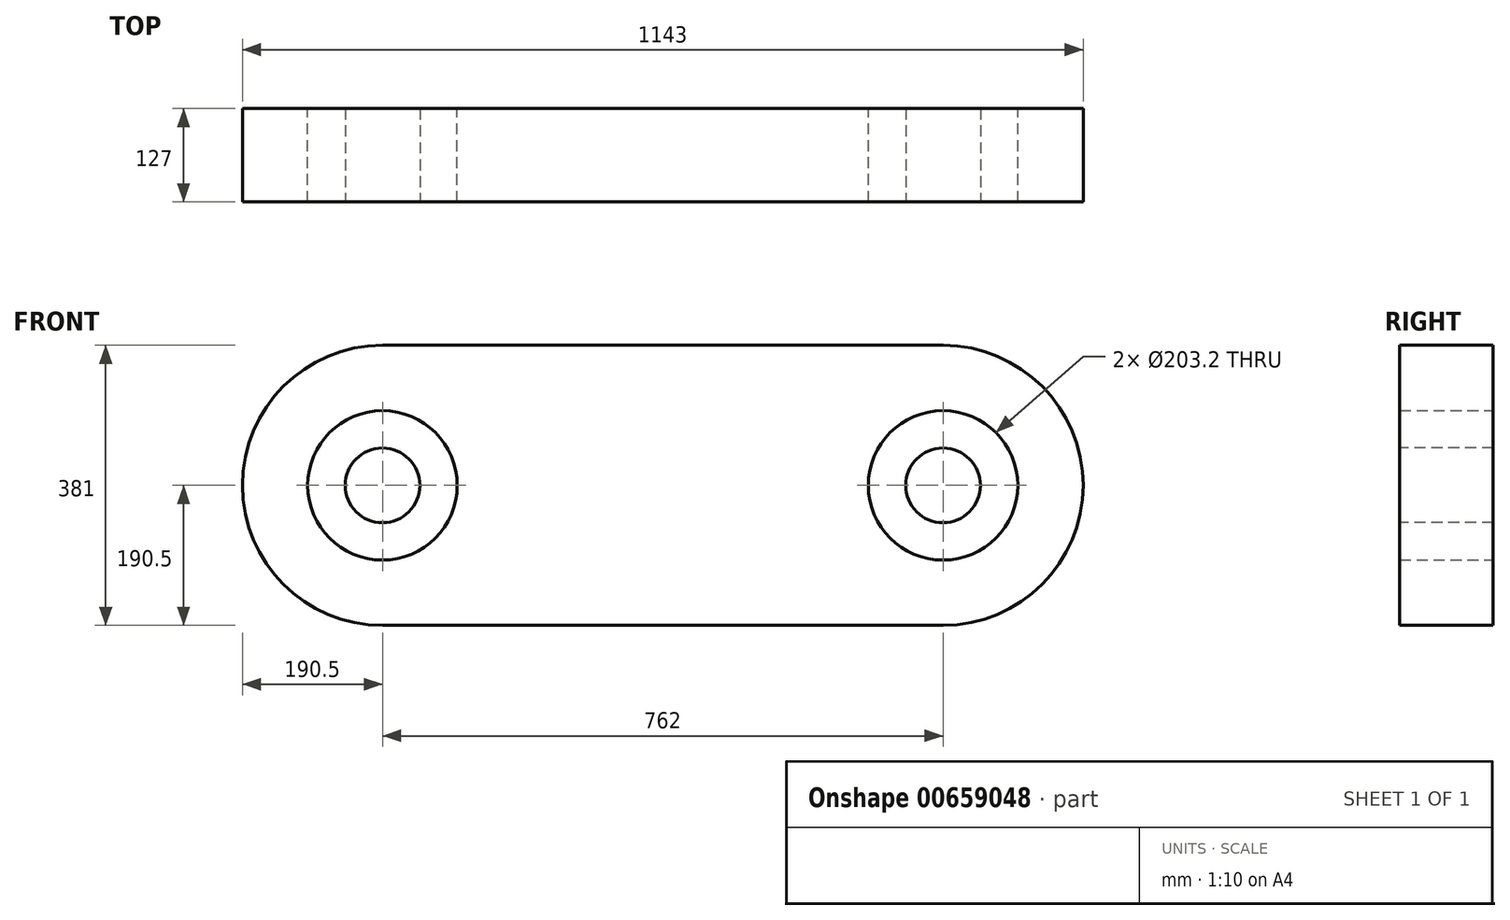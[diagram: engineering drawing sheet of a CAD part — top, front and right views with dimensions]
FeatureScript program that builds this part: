
annotation { "Feature Type Name" : "Feature", "Feature Type Description" : "" }
export const myFeature = defineFeature(function(context is Context, id is Id, definition is map)
    precondition{}
    {
        {
            var Q0;
            Q0=qCreatedBy(makeId("Front.planeOp"),FACE);
            var sketch = newSketch(context, id + "F0", { "sketchPlane" : qUnion([Q0])});
            skArc(sketch, "E0", {"start": v(-381, 190.5) * mm, "mid": v(-571.5, 0) * mm, "end": v(-381, -190.5) * mm});
            skArc(sketch, "E1", {"start": v(381, -190.5) * mm, "mid": v(571.5, 0) * mm, "end": v(381, 190.5) * mm});
            skLineSegment(sketch, "E2", {"start": v(-381, 190.5) * mm, "end": v(381, 190.5) * mm});
            skLineSegment(sketch, "E3", {"start": v(-381, -190.5) * mm, "end": v(381, -190.5) * mm});
            skCircle(sketch, "E4", {"center": v(-381, 0) * mm, "radius": 50.8 * mm});
            skCircle(sketch, "E5", {"center": v(-381, 0) * mm, "radius": 101.6 * mm});
            skCircle(sketch, "E6", {"center": v(381, 0) * mm, "radius": 50.8 * mm});
            skCircle(sketch, "E7", {"center": v(381, 0) * mm, "radius": 101.6 * mm});
            skSolve(sketch);
        }
        {
            var Q0;
            Q0 = qSketchRegion(id + "F0", true);
            extrude(context, id + "F1", {"entities" : qUnion([Q0]), "depth" : 127 * mm, "offsetDistance" : 25.4 * mm});
        }
        {
            var Q0;
            Q0=makeQuery(id+"F1.opExtrude","CAP_FACE",FACE,{"disambiguationData":[OSD([sQuery(id+"F0.wireOp",EDGE,"E0"),sQuery(id+"F0.wireOp",EDGE,"E1"),sQuery(id+"F0.wireOp",EDGE,"E2"),sQuery(id+"F0.wireOp",EDGE,"E3"),sQuery(id+"F0.wireOp",EDGE,"E5"),sQuery(id+"F0.wireOp",EDGE,"E7")])],"isStart":false});
            var sketch = newSketch(context, id + "F2", { "sketchPlane" : qUnion([Q0])});
            skCircle(sketch, "E8", {"center": v(-381, 0) * mm, "radius": 50.8 * mm});
            skCircle(sketch, "E9", {"center": v(381, 0) * mm, "radius": 50.8 * mm});
            skSolve(sketch);
        }
        {
            var Q0;
            Q0 = qSketchRegion(id + "F2", true);
            extrude(context, id + "F3", {"entities" : qUnion([Q0]), "oppositeDirection" : true, "depth" : 127 * mm, "offsetDistance" : 25.4 * mm});
        }
    });
